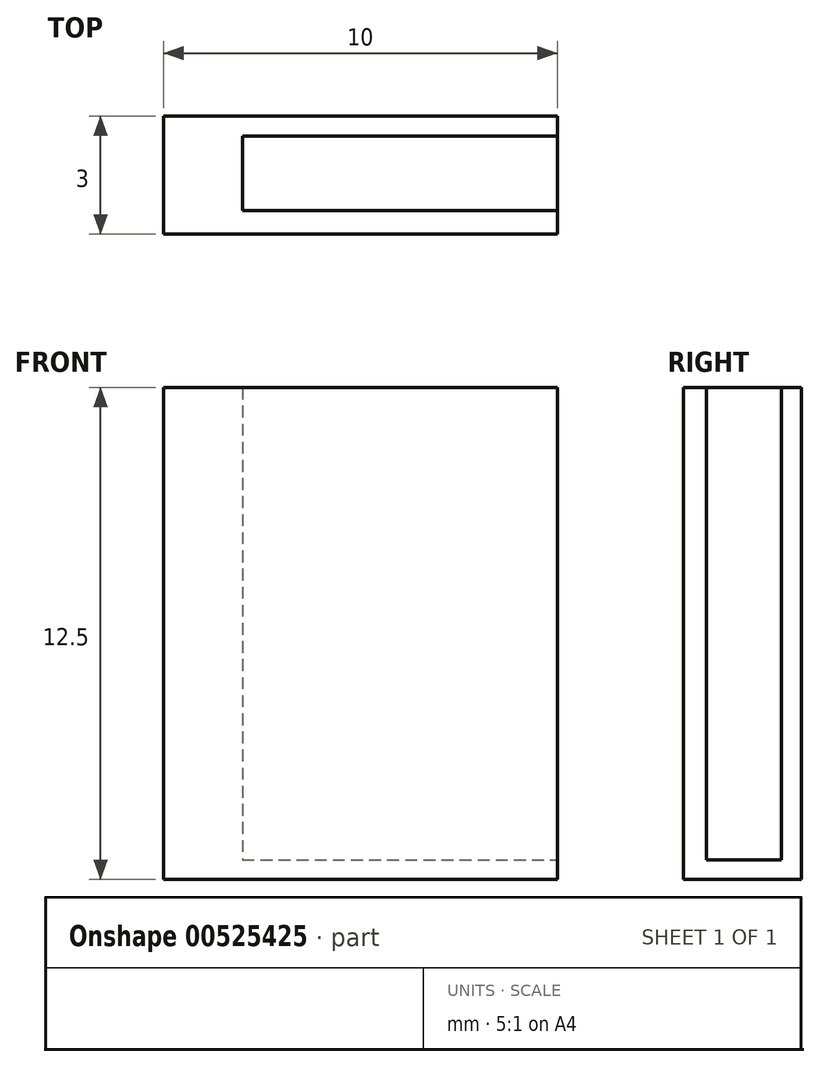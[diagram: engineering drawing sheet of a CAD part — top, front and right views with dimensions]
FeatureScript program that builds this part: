
annotation { "Feature Type Name" : "Feature", "Feature Type Description" : "" }
export const myFeature = defineFeature(function(context is Context, id is Id, definition is map)
    precondition{}
    {
        {
            var Q0;
            Q0=qCreatedBy(makeId("Front.planeOp"),FACE);
            var sketch = newSketch(context, id + "F0", { "sketchPlane" : qUnion([Q0])});
            skLineSegment(sketch, "E0.bottom", {"start": v(0, 0) * mm, "end": v(10, 0) * mm});
            skLineSegment(sketch, "E0.top", {"start": v(0, 12.5) * mm, "end": v(10, 12.5) * mm});
            skLineSegment(sketch, "E0.left", {"start": v(0, 0) * mm, "end": v(0, 12.5) * mm});
            skLineSegment(sketch, "E0.right", {"start": v(10, 0) * mm, "end": v(10, 12.5) * mm});
            skSolve(sketch);
        }
        {
            var Q0;
            Q0 = qSketchRegion(id + "F0", true);
            var Q1;
            Q1 = qSketchRegion(id + "F2", true);
            extrude(context, id + "F1", {"entities" : qUnion([Q0, Q1]), "depth" : 3 * mm, "offsetDistance" : 25 * mm});
        }
        {
            var Q0;
            Q0=makeQuery(id+"F1.opExtrude","SWEPT_FACE",FACE,{"disambiguationData":[OSD([sQuery(id+"F0.wireOp",EDGE,"E0.right")])]});
            var sketch = newSketch(context, id + "F2", { "sketchPlane" : qUnion([Q0])});
            skLineSegment(sketch, "E1.bottom", {"start": v(-2.4, 12.5) * mm, "end": v(-0.5, 12.5) * mm});
            skLineSegment(sketch, "E1.top", {"start": v(-2.4, 0.5) * mm, "end": v(-0.5, 0.5) * mm});
            skLineSegment(sketch, "E1.left", {"start": v(-2.4, 12.5) * mm, "end": v(-2.4, 0.5) * mm});
            skLineSegment(sketch, "E1.right", {"start": v(-0.5, 12.5) * mm, "end": v(-0.5, 0.5) * mm});
            skSolve(sketch);
        }
        {
            var Q0;
            Q0=makeQuery(id+"F2.imprint","IMPRINT",FACE,{"disambiguationData":[TD([[makeQuery(id+"F2.imprint","IMPRINT",EDGE,{"derivedFrom":sQuery(id+"F2.wireOp",EDGE,"E1.bottom")}),-1.0]])]});
            extrude(context, id + "F3", {"entities" : qUnion([Q0]), "operationType" : NewBodyOperationType.REMOVE, "depth" : -8 * mm, "offsetDistance" : 25 * mm});
        }
    });
